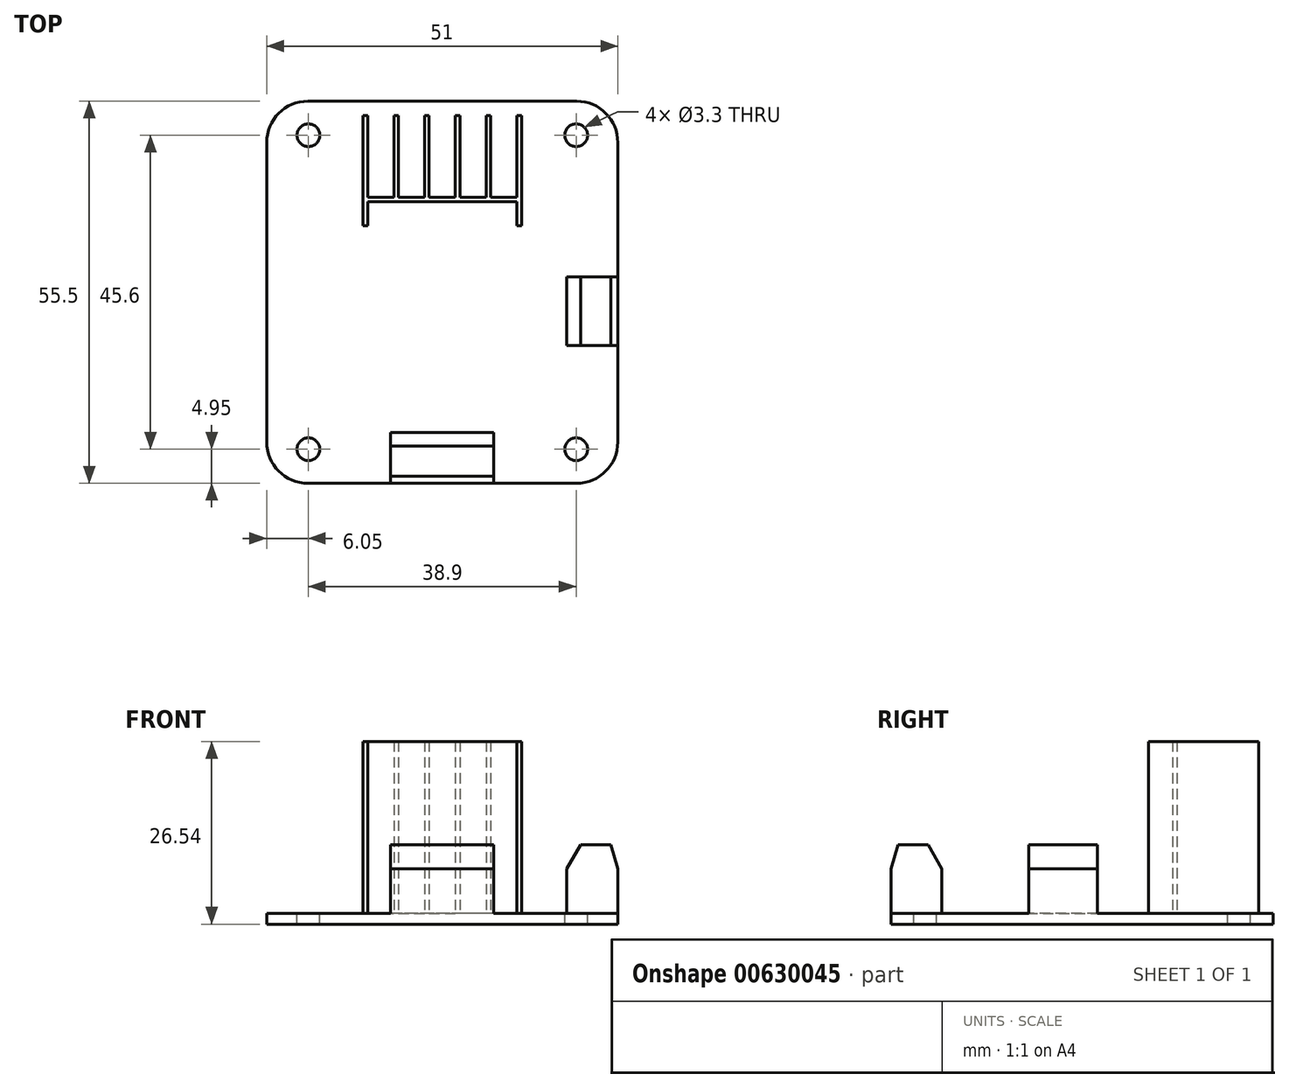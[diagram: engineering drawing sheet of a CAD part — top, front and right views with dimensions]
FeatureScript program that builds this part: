
annotation { "Feature Type Name" : "Feature", "Feature Type Description" : "" }
export const myFeature = defineFeature(function(context is Context, id is Id, definition is map)
    precondition{}
    {
        {
            var Q0;
            Q0=qCreatedBy(makeId("Top.planeOp"),FACE);
            var sketch = newSketch(context, id + "F0", { "sketchPlane" : qUnion([Q0])});
            skLineSegment(sketch, "E0.bottom", {"start": v(19.5, -27.75) * mm, "end": v(-19.5, -27.75) * mm});
            skLineSegment(sketch, "E0.top", {"start": v(19.5, 27.75) * mm, "end": v(-19.5, 27.75) * mm});
            skLineSegment(sketch, "E0.left", {"start": v(25.5, -21.75) * mm, "end": v(25.5, 21.75) * mm});
            skLineSegment(sketch, "E0.right", {"start": v(-25.5, -21.75) * mm, "end": v(-25.5, 21.75) * mm});
            skPoint(sketch, "E0.middle", {"position": v(0, 0) * mm});
            skPoint(sketch, "E1.visualSharp", {"position": v(-25.5, 27.75) * mm});
            skArc(sketch, "E1.filletArc", {"start": v(-19.5, 27.75) * mm, "mid": v(-23.74, 26) * mm, "end": v(-25.5, 21.75) * mm});
            skPoint(sketch, "E2.visualSharp", {"position": v(25.5, 27.75) * mm});
            skArc(sketch, "E2.filletArc", {"start": v(25.5, 21.75) * mm, "mid": v(23.74, 26) * mm, "end": v(19.5, 27.75) * mm});
            skPoint(sketch, "E3.visualSharp", {"position": v(25.5, -27.75) * mm});
            skArc(sketch, "E3.filletArc", {"start": v(19.5, -27.75) * mm, "mid": v(23.74, -26) * mm, "end": v(25.5, -21.75) * mm});
            skPoint(sketch, "E4.visualSharp", {"position": v(-25.5, -27.75) * mm});
            skArc(sketch, "E4.filletArc", {"start": v(-25.5, -21.75) * mm, "mid": v(-23.74, -26) * mm, "end": v(-19.5, -27.75) * mm});
            skSolve(sketch);
        }
        {
            var Q0;
            Q0 = qSketchRegion(id + "F0", true);
            extrude(context, id + "F1", {"entities" : qUnion([Q0]), "depth" : 1.54 * mm, "offsetDistance" : 25 * mm});
        }
        {
            var Q0;
            Q0=makeQuery(id+"F1.opExtrude","CAP_FACE",FACE,{"disambiguationData":[OSD([sQuery(id+"F0.wireOp",EDGE,"E0.bottom"),sQuery(id+"F0.wireOp",EDGE,"E0.top"),sQuery(id+"F0.wireOp",EDGE,"E0.left"),sQuery(id+"F0.wireOp",EDGE,"E0.right")])],"isStart":false});
            var sketch = newSketch(context, id + "F2", { "sketchPlane" : qUnion([Q0])});
            skLineSegment(sketch, "E5.bottom", {"start": v(19.45, -22.8) * mm, "end": v(-19.45, -22.8) * mm, "construction": true});
            skLineSegment(sketch, "E5.top", {"start": v(19.45, 22.8) * mm, "end": v(-19.45, 22.8) * mm, "construction": true});
            skLineSegment(sketch, "E5.left", {"start": v(19.45, -22.8) * mm, "end": v(19.45, 22.8) * mm, "construction": true});
            skLineSegment(sketch, "E5.right", {"start": v(-19.45, -22.8) * mm, "end": v(-19.45, 22.8) * mm, "construction": true});
            skPoint(sketch, "E5.middle", {"position": v(0, 0) * mm});
            skSolve(sketch);
        }
        {
            var Q0;
            Q0=sQuery(id+"F2.wireOp",VERTEX,"E5.top.end");
            var Q1;
            Q1=sQuery(id+"F2.wireOp",VERTEX,"E5.left.end");
            var Q2;
            Q2=sQuery(id+"F2.wireOp",VERTEX,"E5.bottom.end");
            var Q3;
            Q3=sQuery(id+"F2.wireOp",VERTEX,"E5.left.start");
            var Q4;
            Q4=makeQuery(id+"F1.opExtrude","SWEPT_BODY",BODY,{"disambiguationData":[OSD([sQuery(id+"F0.wireOp",EDGE,"E0.bottom"),sQuery(id+"F0.wireOp",EDGE,"E0.top"),sQuery(id+"F0.wireOp",EDGE,"E0.left"),sQuery(id+"F0.wireOp",EDGE,"E0.right")])]});
            hole(context, id + "F3", {"style" : HoleStyle.SIMPLE, "endStyle" : HoleEndStyle.THROUGH, "holeDiameter" : 3.3 * mm, "majorDiameter" : 5 * mm, "tappedDepth" : 12 * mm, "tapClearance" : 3, "locations" : qUnion([Q0, Q1, Q2, Q3]), "scope" : qUnion([Q4])});
        }
        {
            var Q0;
            Q0=makeQuery(id+"F1.opExtrude","CAP_FACE",FACE,{"disambiguationData":[OSD([sQuery(id+"F0.wireOp",EDGE,"E0.bottom"),sQuery(id+"F0.wireOp",EDGE,"E0.top"),sQuery(id+"F0.wireOp",EDGE,"E0.left"),sQuery(id+"F0.wireOp",EDGE,"E0.right"),sQuery(id+"F0.wireOp",EDGE,"E1.filletArc"),sQuery(id+"F0.wireOp",EDGE,"E2.filletArc"),sQuery(id+"F0.wireOp",EDGE,"E3.filletArc"),sQuery(id+"F0.wireOp",EDGE,"E4.filletArc")])],"isStart":false});
            var sketch = newSketch(context, id + "F4", { "sketchPlane" : qUnion([Q0])});
            skLineSegment(sketch, "E6.bottom", {"start": v(11.5, 9.65) * mm, "end": v(10.85, 9.65) * mm});
            skLineSegment(sketch, "E6.top", {"start": v(11.5, 25.65) * mm, "end": v(10.85, 25.65) * mm});
            skLineSegment(sketch, "E6.left", {"start": v(11.5, 9.65) * mm, "end": v(11.5, 25.65) * mm});
            skLineSegment(sketch, "E6.right", {"start": v(-11.5, 9.65) * mm, "end": v(-11.5, 25.65) * mm});
            skPoint(sketch, "E6.middle", {"position": v(0, 17.65) * mm});
            skLineSegment(sketch, "E7", {"start": v(-10.85, 25.65) * mm, "end": v(-10.85, 13.8) * mm});
            skLineSegment(sketch, "E8", {"start": v(-10.85, 13.8) * mm, "end": v(-7.03, 13.8) * mm});
            skLineSegment(sketch, "E9", {"start": v(-7.03, 13.8) * mm, "end": v(-7.03, 25.65) * mm});
            skLineSegment(sketch, "E10", {"start": v(-6.38, 25.65) * mm, "end": v(-6.38, 13.8) * mm});
            skLineSegment(sketch, "E11", {"start": v(-6.38, 13.8) * mm, "end": v(-2.56, 13.8) * mm});
            skLineSegment(sketch, "E12", {"start": v(-2.56, 13.8) * mm, "end": v(-2.56, 25.65) * mm});
            skLineSegment(sketch, "E13", {"start": v(-1.9, 25.65) * mm, "end": v(-1.9, 13.8) * mm});
            skLineSegment(sketch, "E14.MirrorCS", {"start": v(1.9, 25.65) * mm, "end": v(1.9, 13.8) * mm});
            skLineSegment(sketch, "E15.MirrorCS", {"start": v(2.56, 13.8) * mm, "end": v(2.56, 25.65) * mm});
            skLineSegment(sketch, "E16.MirrorCS", {"start": v(6.38, 13.8) * mm, "end": v(2.56, 13.8) * mm});
            skLineSegment(sketch, "E17.MirrorCS", {"start": v(6.38, 25.65) * mm, "end": v(6.38, 13.8) * mm});
            skLineSegment(sketch, "E18.MirrorCS", {"start": v(7.03, 13.8) * mm, "end": v(7.03, 25.65) * mm});
            skLineSegment(sketch, "E19.MirrorCS", {"start": v(10.85, 13.8) * mm, "end": v(7.03, 13.8) * mm});
            skLineSegment(sketch, "E20.MirrorCS", {"start": v(10.85, 25.65) * mm, "end": v(10.85, 13.8) * mm});
            skLineSegment(sketch, "E21.trimOffspring", {"start": v(-10.85, 25.65) * mm, "end": v(-11.5, 25.65) * mm});
            skLineSegment(sketch, "E22.trimOffspring", {"start": v(-6.38, 25.65) * mm, "end": v(-7.03, 25.65) * mm});
            skLineSegment(sketch, "E23.trimOffspring", {"start": v(-1.9, 25.65) * mm, "end": v(-2.56, 25.65) * mm});
            skLineSegment(sketch, "E24.trimOffspring", {"start": v(7.03, 25.65) * mm, "end": v(6.38, 25.65) * mm});
            skLineSegment(sketch, "E25.trimOffspring", {"start": v(2.56, 25.65) * mm, "end": v(1.9, 25.65) * mm});
            skPoint(sketch, "E26.MirrorCS.end.orphan", {"position": v(0, 13.8) * mm});
            skPoint(sketch, "E26.MirrorCS.start.orphan", {"position": v(1.9, 13.8) * mm});
            skLineSegment(sketch, "E27", {"start": v(-1.9, 13.8) * mm, "end": v(1.9, 13.8) * mm});
            skLineSegment(sketch, "E28", {"start": v(-10.85, 9.65) * mm, "end": v(-10.85, 13.15) * mm});
            skLineSegment(sketch, "E29", {"start": v(-10.85, 13.15) * mm, "end": v(10.85, 13.15) * mm});
            skLineSegment(sketch, "E30", {"start": v(10.85, 13.15) * mm, "end": v(10.85, 9.65) * mm});
            skLineSegment(sketch, "E31.trimOffspring", {"start": v(-10.85, 9.65) * mm, "end": v(-11.5, 9.65) * mm});
            skSolve(sketch);
        }
        {
            var Q0;
            Q0 = qSketchRegion(id + "F4", true);
            extrude(context, id + "F5", {"entities" : qUnion([Q0]), "operationType" : NewBodyOperationType.ADD, "depth" : 25 * mm, "offsetDistance" : 25 * mm});
        }
        {
            var Q0;
            Q0=makeQuery(id+"F1.opExtrude","SWEPT_FACE",FACE,{"disambiguationData":[OSD([sQuery(id+"F0.wireOp",EDGE,"E0.bottom")])]});
            cPlane(context, id + "F6", {"entities" : qUnion([Q0]), "cplaneType" : CPlaneType.OFFSET, "offset" : 20 * mm, "oppositeDirection" : true, "width" : 150 * mm, "height" : 150 * mm});
        }
        {
            var Q0;
            Q0=qCreatedBy(id+"F6.planeOp",FACE);
            var sketch = newSketch(context, id + "F7", { "sketchPlane" : qUnion([Q0])});
            skPoint(sketch, "E32.0", {"position": v(25.5, 1.54) * mm});
            skLineSegment(sketch, "E33.bottom", {"start": v(25.5, 1.54) * mm, "end": v(18.1, 1.54) * mm});
            skLineSegment(sketch, "E33.top", {"start": v(24.5, 11.54) * mm, "end": v(20.1, 11.54) * mm});
            skLineSegment(sketch, "E33.left", {"start": v(25.5, 1.54) * mm, "end": v(25.5, 8.04) * mm});
            skLineSegment(sketch, "E33.right", {"start": v(18.1, 1.54) * mm, "end": v(18.1, 8.04) * mm});
            skLineSegment(sketch, "E34", {"start": v(24.5, 11.54) * mm, "end": v(25.5, 8.04) * mm});
            skPoint(sketch, "E35.orphan", {"position": v(25.5, 11.54) * mm});
            skLineSegment(sketch, "E36", {"start": v(20.1, 11.54) * mm, "end": v(18.1, 8.04) * mm});
            skPoint(sketch, "E37.orphan", {"position": v(18.1, 11.54) * mm});
            skSolve(sketch);
        }
        {
            var Q0;
            Q0=makeQuery(id+"F7.imprint","IMPRINT",FACE,{"disambiguationData":[TD([[makeQuery(id+"F7.imprint","IMPRINT",EDGE,{"derivedFrom":sQuery(id+"F7.wireOp",EDGE,"E33.bottom")}),-1.0]])]});
            extrude(context, id + "F8", {"entities" : qUnion([Q0]), "operationType" : NewBodyOperationType.ADD, "oppositeDirection" : true, "depth" : 10 * mm, "offsetDistance" : 25 * mm});
        }
        {
            var Q0;
            Q0=qCreatedBy(makeId("Right.planeOp"),FACE);
            var sketch = newSketch(context, id + "F9", { "sketchPlane" : qUnion([Q0])});
            skPoint(sketch, "E38.0", {"position": v(-20.35, 1.54) * mm});
            skLineSegment(sketch, "E39.bottom", {"start": v(-20.35, 1.54) * mm, "end": v(-27.75, 1.54) * mm});
            skLineSegment(sketch, "E39.top", {"start": v(-22.35, 11.54) * mm, "end": v(-26.75, 11.54) * mm});
            skLineSegment(sketch, "E39.left", {"start": v(-20.35, 1.54) * mm, "end": v(-20.35, 8.04) * mm});
            skLineSegment(sketch, "E39.right", {"start": v(-27.75, 1.54) * mm, "end": v(-27.75, 8.04) * mm});
            skLineSegment(sketch, "E40", {"start": v(-22.35, 11.54) * mm, "end": v(-20.35, 8.04) * mm});
            skPoint(sketch, "E41.orphan", {"position": v(-20.35, 11.54) * mm});
            skLineSegment(sketch, "E42", {"start": v(-26.75, 11.54) * mm, "end": v(-27.75, 8.04) * mm});
            skPoint(sketch, "E43.orphan", {"position": v(-27.75, 11.54) * mm});
            skSolve(sketch);
        }
        {
            var Q0;
            Q0=makeQuery(id+"F9.imprint","IMPRINT",FACE,{"disambiguationData":[TD([[makeQuery(id+"F9.imprint","IMPRINT",EDGE,{"derivedFrom":sQuery(id+"F9.wireOp",EDGE,"E39.bottom")}),-1.0]])]});
            extrude(context, id + "F10", {"entities" : qUnion([Q0]), "operationType" : NewBodyOperationType.ADD, "endBound" : BoundingType.SYMMETRIC, "depth" : 15 * mm, "offsetDistance" : 25 * mm});
        }
    });
